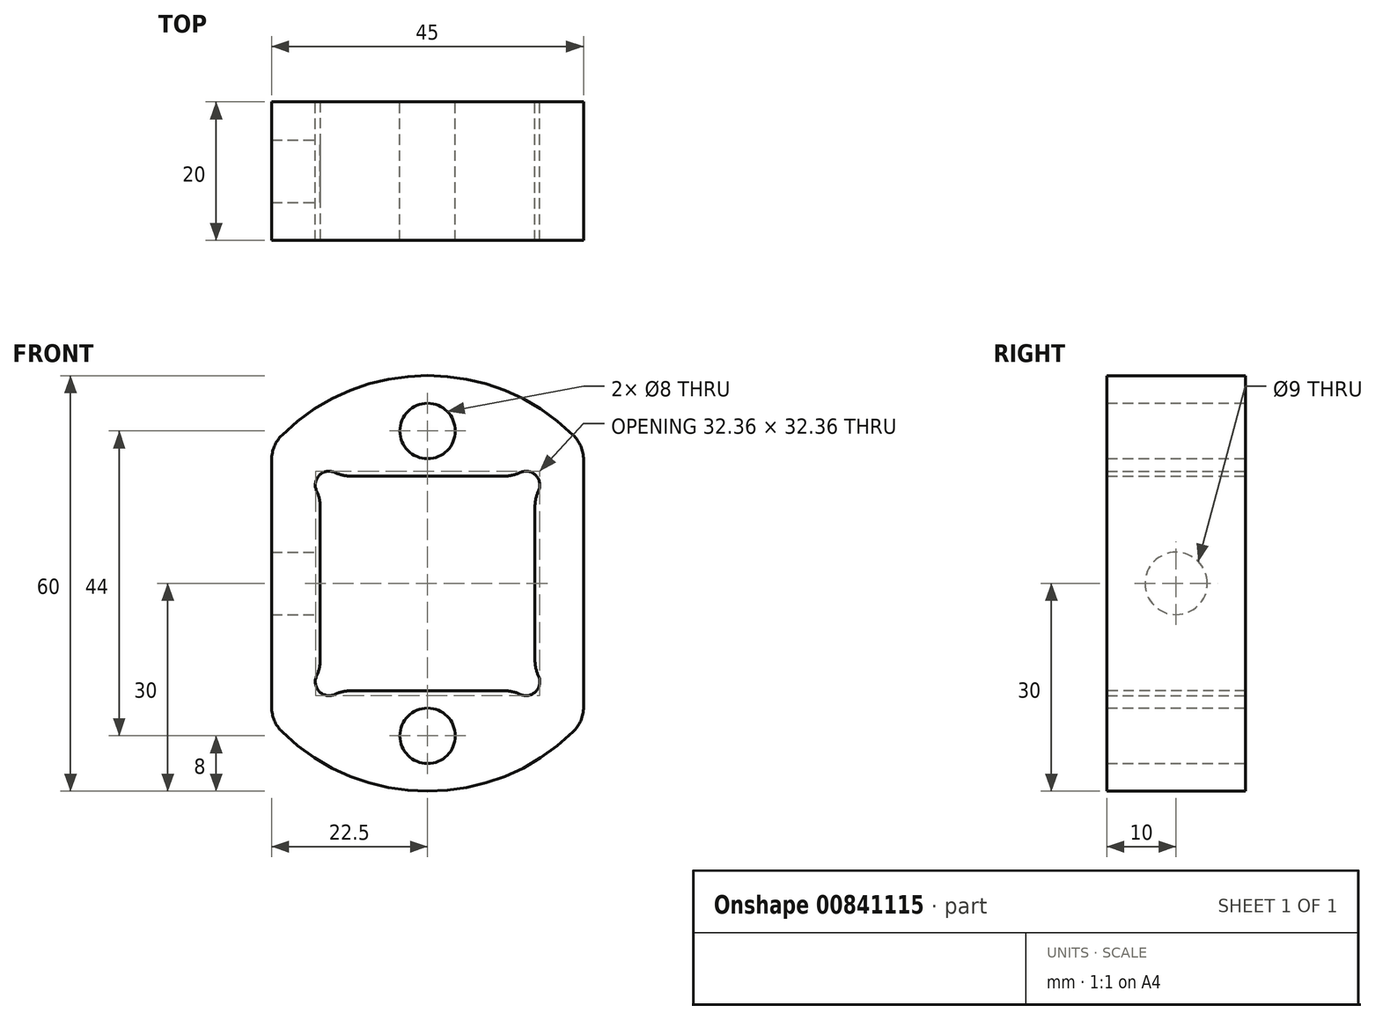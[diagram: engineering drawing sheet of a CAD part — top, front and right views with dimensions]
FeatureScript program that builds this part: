
annotation { "Feature Type Name" : "Feature", "Feature Type Description" : "" }
export const myFeature = defineFeature(function(context is Context, id is Id, definition is map)
    precondition{}
    {
        {
            var Q0;
            Q0=qCreatedBy(makeId("Front.planeOp"),FACE);
            var sketch = newSketch(context, id + "F0", { "sketchPlane" : qUnion([Q0])});
            skCircle(sketch, "E0", {"center": v(0, 0) * mm, "radius": 30 * mm});
            skLineSegment(sketch, "E1.bottom", {"start": v(15.5, -15.5) * mm, "end": v(-15.5, -15.5) * mm});
            skLineSegment(sketch, "E1.top", {"start": v(15.5, 15.5) * mm, "end": v(-15.5, 15.5) * mm});
            skLineSegment(sketch, "E1.left", {"start": v(15.5, -15.5) * mm, "end": v(15.5, 15.5) * mm});
            skLineSegment(sketch, "E1.right", {"start": v(-15.5, -15.5) * mm, "end": v(-15.5, 15.5) * mm});
            skSolve(sketch);
        }
        {
            var Q0;
            Q0=makeQuery(id+"F0.imprint","IMPRINT",FACE,{"disambiguationData":[TD([[makeQuery(id+"F0.imprint","IMPRINT",EDGE,{"derivedFrom":sQuery(id+"F0.wireOp",EDGE,"E0")}),1.0]])]});
            extrude(context, id + "F1", {"entities" : qUnion([Q0]), "depth" : 20 * mm, "offsetDistance" : 25 * mm});
        }
        {
            var Q0;
            Q0=qCreatedBy(makeId("Front.planeOp"),FACE);
            var sketch = newSketch(context, id + "F2", { "sketchPlane" : qUnion([Q0])});
            skCircle(sketch, "E2", {"center": v(0, 22) * mm, "radius": 4 * mm});
            skCircle(sketch, "E3.MirrorC", {"center": v(0, -22) * mm, "radius": 4 * mm});
            skSolve(sketch);
        }
        {
            var Q0;
            Q0 = qSketchRegion(id + "F2", true);
            extrude(context, id + "F3", {"entities" : qUnion([Q0]), "operationType" : NewBodyOperationType.REMOVE, "depth" : 48.3 * mm, "offsetDistance" : 25 * mm});
        }
        {
            var Q0;
            Q0=qCreatedBy(makeId("Front.planeOp"),FACE);
            var sketch = newSketch(context, id + "F4", { "sketchPlane" : qUnion([Q0])});
            skLineSegment(sketch, "E4.bottom", {"start": v(22.5, -40) * mm, "end": v(-22.5, -40) * mm, "construction": true});
            skLineSegment(sketch, "E4.top", {"start": v(22.5, 40) * mm, "end": v(-22.5, 40) * mm, "construction": true});
            skLineSegment(sketch, "E4.left", {"start": v(22.5, -40) * mm, "end": v(22.5, 40) * mm});
            skLineSegment(sketch, "E4.right", {"start": v(-22.5, -40) * mm, "end": v(-22.5, 40) * mm});
            skPoint(sketch, "E4.middle", {"position": v(0, 0) * mm});
            skLineSegment(sketch, "E5.bottom", {"start": v(22.5, 40) * mm, "end": v(58.19, 40) * mm});
            skLineSegment(sketch, "E5.top", {"start": v(22.5, -40) * mm, "end": v(58.19, -40) * mm});
            skLineSegment(sketch, "E5.left", {"start": v(22.5, 40) * mm, "end": v(22.5, -40) * mm, "construction": true});
            skLineSegment(sketch, "E5.right", {"start": v(58.19, 40) * mm, "end": v(58.19, -40) * mm});
            skLineSegment(sketch, "E6.bottom", {"start": v(-22.5, 40) * mm, "end": v(-69.93, 40) * mm});
            skLineSegment(sketch, "E6.top", {"start": v(-22.5, -40) * mm, "end": v(-69.93, -40) * mm});
            skLineSegment(sketch, "E6.left", {"start": v(-22.5, 40) * mm, "end": v(-22.5, -40) * mm, "construction": true});
            skLineSegment(sketch, "E6.right", {"start": v(-69.93, 40) * mm, "end": v(-69.93, -40) * mm});
            skSolve(sketch);
        }
        {
            var Q0;
            Q0=makeQuery(id+"F4.imprint","IMPRINT",FACE,{"disambiguationData":[TD([[makeQuery(id+"F4.imprint","IMPRINT",EDGE,{"derivedFrom":sQuery(id+"F4.wireOp",EDGE,"E4.right")}),1.0]])]});
            var Q1;
            Q1=makeQuery(id+"F4.imprint","IMPRINT",FACE,{"disambiguationData":[TD([[makeQuery(id+"F4.imprint","IMPRINT",EDGE,{"derivedFrom":sQuery(id+"F4.wireOp",EDGE,"E4.left")}),-1.0]])]});
            extrude(context, id + "F5", {"entities" : qUnion([Q0, Q1]), "operationType" : NewBodyOperationType.REMOVE, "depth" : 29.8 * mm, "offsetDistance" : 25 * mm});
        }
        {
            var Q0;
            Q0=qCreatedBy(makeId("Right.planeOp"),FACE);
            var sketch = newSketch(context, id + "F6", { "sketchPlane" : qUnion([Q0])});
            skCircle(sketch, "E7", {"center": v(-10, 0) * mm, "radius": 4.5 * mm});
            skSolve(sketch);
        }
        {
            var Q0;
            Q0 = qSketchRegion(id + "F6", true);
            extrude(context, id + "F7", {"entities" : qUnion([Q0]), "operationType" : NewBodyOperationType.REMOVE, "endBound" : BoundingType.THROUGH_ALL, "oppositeDirection" : true, "depth" : 25 * mm, "offsetDistance" : 25 * mm});
        }
        {
            var Q0;
            Q0=qCreatedBy(makeId("Front.planeOp"),FACE);
            var sketch = newSketch(context, id + "F8", { "sketchPlane" : qUnion([Q0])});
            skCircle(sketch, "E8", {"center": v(-14.2, 14.2) * mm, "radius": 2 * mm});
            skCircle(sketch, "E9.MirrorC", {"center": v(14.2, 14.2) * mm, "radius": 2 * mm});
            skCircle(sketch, "E10.MirrorC", {"center": v(-14.2, -14.2) * mm, "radius": 2 * mm});
            skCircle(sketch, "E11.MirrorC", {"center": v(14.2, -14.2) * mm, "radius": 2 * mm});
            skSolve(sketch);
        }
        {
            var Q0;
            Q0 = qSketchRegion(id + "F8", true);
            extrude(context, id + "F9", {"entities" : qUnion([Q0]), "operationType" : NewBodyOperationType.REMOVE, "endBound" : BoundingType.THROUGH_ALL, "depth" : 25 * mm, "offsetDistance" : 25 * mm});
        }
        {
            var Q0;
            Q0=makeQuery(id+"F9.boolean.opBoolean","INTERSECT",EDGE,{"derivedFrom":[makeQuery(id+"F1.opExtrude","SWEPT_FACE",FACE,{"disambiguationData":[OSD([sQuery(id+"F0.wireOp",EDGE,"E1.top")])]}),makeQuery(id+"F9.opExtrude","SWEPT_FACE",FACE,{"disambiguationData":[OSD([sQuery(id+"F8.wireOp",EDGE,"E8")])]})]});
            var Q1;
            Q1=makeQuery(id+"F9.boolean.opBoolean","INTERSECT",EDGE,{"derivedFrom":[makeQuery(id+"F1.opExtrude","SWEPT_FACE",FACE,{"disambiguationData":[OSD([sQuery(id+"F0.wireOp",EDGE,"E1.right")])]}),makeQuery(id+"F9.opExtrude","SWEPT_FACE",FACE,{"disambiguationData":[OSD([sQuery(id+"F8.wireOp",EDGE,"E8")])]})]});
            var Q2;
            Q2=makeQuery(id+"F9.boolean.opBoolean","INTERSECT",EDGE,{"derivedFrom":[makeQuery(id+"F1.opExtrude","SWEPT_FACE",FACE,{"disambiguationData":[OSD([sQuery(id+"F0.wireOp",EDGE,"E1.top")])]}),makeQuery(id+"F9.opExtrude","SWEPT_FACE",FACE,{"disambiguationData":[OSD([sQuery(id+"F8.wireOp",EDGE,"E9.MirrorC")])]})]});
            var Q3;
            Q3=makeQuery(id+"F9.boolean.opBoolean","INTERSECT",EDGE,{"derivedFrom":[makeQuery(id+"F1.opExtrude","SWEPT_FACE",FACE,{"disambiguationData":[OSD([sQuery(id+"F0.wireOp",EDGE,"E1.left")])]}),makeQuery(id+"F9.opExtrude","SWEPT_FACE",FACE,{"disambiguationData":[OSD([sQuery(id+"F8.wireOp",EDGE,"E9.MirrorC")])]})]});
            var Q4;
            Q4=makeQuery(id+"F9.boolean.opBoolean","INTERSECT",EDGE,{"derivedFrom":[makeQuery(id+"F1.opExtrude","SWEPT_FACE",FACE,{"disambiguationData":[OSD([sQuery(id+"F0.wireOp",EDGE,"E1.left")])]}),makeQuery(id+"F9.opExtrude","SWEPT_FACE",FACE,{"disambiguationData":[OSD([sQuery(id+"F8.wireOp",EDGE,"E11.MirrorC")])]})]});
            var Q5;
            Q5=makeQuery(id+"F9.boolean.opBoolean","INTERSECT",EDGE,{"derivedFrom":[makeQuery(id+"F1.opExtrude","SWEPT_FACE",FACE,{"disambiguationData":[OSD([sQuery(id+"F0.wireOp",EDGE,"E1.bottom")])]}),makeQuery(id+"F9.opExtrude","SWEPT_FACE",FACE,{"disambiguationData":[OSD([sQuery(id+"F8.wireOp",EDGE,"E11.MirrorC")])]})]});
            var Q6;
            Q6=makeQuery(id+"F9.boolean.opBoolean","INTERSECT",EDGE,{"derivedFrom":[makeQuery(id+"F1.opExtrude","SWEPT_FACE",FACE,{"disambiguationData":[OSD([sQuery(id+"F0.wireOp",EDGE,"E1.bottom")])]}),makeQuery(id+"F9.opExtrude","SWEPT_FACE",FACE,{"disambiguationData":[OSD([sQuery(id+"F8.wireOp",EDGE,"E10.MirrorC")])]})]});
            var Q7;
            Q7=makeQuery(id+"F9.boolean.opBoolean","INTERSECT",EDGE,{"derivedFrom":[makeQuery(id+"F1.opExtrude","SWEPT_FACE",FACE,{"disambiguationData":[OSD([sQuery(id+"F0.wireOp",EDGE,"E1.right")])]}),makeQuery(id+"F9.opExtrude","SWEPT_FACE",FACE,{"disambiguationData":[OSD([sQuery(id+"F8.wireOp",EDGE,"E10.MirrorC")])]})]});
            fillet(context, id + "F10", {"entities" : qUnion([Q0, Q1, Q2, Q3, Q4, Q5, Q6, Q7]), "radius" : 5 * mm, "tangentPropagation" : true, "allowEdgeOverflow" : false});
        }
        {
            var Q0;
            Q0=makeQuery(id+"F5.boolean.opBoolean","INTERSECT",EDGE,{"disambiguationData":[OD(1.0)],"derivedFrom":[makeQuery(id+"F1.opExtrude","SWEPT_FACE",FACE,{"disambiguationData":[OSD([sQuery(id+"F0.wireOp",EDGE,"E0")])]}),makeQuery(id+"F5.opExtrude","SWEPT_FACE",FACE,{"disambiguationData":[OSD([sQuery(id+"F4.wireOp",EDGE,"E4.right")])]})]});
            var Q1;
            Q1=makeQuery(id+"F5.boolean.opBoolean","INTERSECT",EDGE,{"disambiguationData":[OD(0.0)],"derivedFrom":[makeQuery(id+"F1.opExtrude","SWEPT_FACE",FACE,{"disambiguationData":[OSD([sQuery(id+"F0.wireOp",EDGE,"E0")])]}),makeQuery(id+"F5.opExtrude","SWEPT_FACE",FACE,{"disambiguationData":[OSD([sQuery(id+"F4.wireOp",EDGE,"E4.right")])]})]});
            var Q2;
            Q2=makeQuery(id+"F5.boolean.opBoolean","INTERSECT",EDGE,{"disambiguationData":[OD(0.0)],"derivedFrom":[makeQuery(id+"F1.opExtrude","SWEPT_FACE",FACE,{"disambiguationData":[OSD([sQuery(id+"F0.wireOp",EDGE,"E0")])]}),makeQuery(id+"F5.opExtrude","SWEPT_FACE",FACE,{"disambiguationData":[OSD([sQuery(id+"F4.wireOp",EDGE,"E4.left")])]})]});
            var Q3;
            Q3=makeQuery(id+"F5.boolean.opBoolean","INTERSECT",EDGE,{"disambiguationData":[OD(1.0)],"derivedFrom":[makeQuery(id+"F1.opExtrude","SWEPT_FACE",FACE,{"disambiguationData":[OSD([sQuery(id+"F0.wireOp",EDGE,"E0")])]}),makeQuery(id+"F5.opExtrude","SWEPT_FACE",FACE,{"disambiguationData":[OSD([sQuery(id+"F4.wireOp",EDGE,"E4.left")])]})]});
            fillet(context, id + "F11", {"entities" : qUnion([Q0, Q1, Q2, Q3]), "radius" : 5 * mm, "tangentPropagation" : true, "allowEdgeOverflow" : false});
        }
    });
